# Revit family: VL2P-GLS150xWS840BU1500
name_source: partatom
category: Leuchten
units: mm (PartAtom-declared; Revit-internal decimal feet)

## family parameters
Basisbauteil = Fläche
Beim Laden mit Abzugskörper schneiden = Nein
Bemaßung runder Anschluss = Durchmesser verwenden
Gemeinsam genutzt = Nein
Lichtquelle = Ja
OmniClass-Nummer = 23.80.70.11
OmniClass-Titel = Luminaries for Internal Lighting
Raumberechnungspunkt = Nein
Teiletyp = Normal

## types (4) — shared parameters
Baugruppenkennzeichen = D5020200
Datei für fotometrisches Netz = VL2_GLS_1502_BU.IES
Emissionsform beim Rendern sichtbar = Nein
Farbfilter = 16777215
Farbtemperaturverschiebung bei Dämpfen der Lampe = <Keine Auswahl>
Hersteller = RIDI Leuchten GmbH
Lampe = LED
Neigungswinkel = 90.00°
URL = www.ridi.de
Von Breite des Rechtecks ausssenden = 1469 mm  [stored 4.81955 ft]
Von Länge des Rechtecks aussenden = 61 mm  [stored 0.200131 ft]
brand = RIDI
conformity mark = CE
electrical safety class = 1
height = 64 mm  [stored 0.209974 ft]
ingress protection (IP) code = IP54
length = 1500 mm  [stored 4.92126 ft]
nominal frequency = 50-60Hz
nominal voltage = 230
voltage type (AC, DC, UC) = AC
weight = 2,6kg
width = 67 mm
zero-valued in all types: Vorgabe-Ansicht

## per-type parameters (varying)
| type | Modell | Scheinlast | rated input power |
| VL2P-GLS150-5FLWS840BU1500 | 2550095 | 84 VA | 84 |
| VL2P-GLS150-7DAWS840BU1500 | 2560095 | 83 VA | 83 |
| VL2P-GLS150-5FLWS865BU1500 | 2550108 | 84 VA | 84 |
| VL2P-GLS150-7DAWS865BU1500 | 2560108 | 87 VA | 87 |

note: column(s) folded — value = type name in every type: product name

note: [stored X ft] marks values corroborated as IEEE doubles in the binary element streams (Revit-internal decimal feet)
